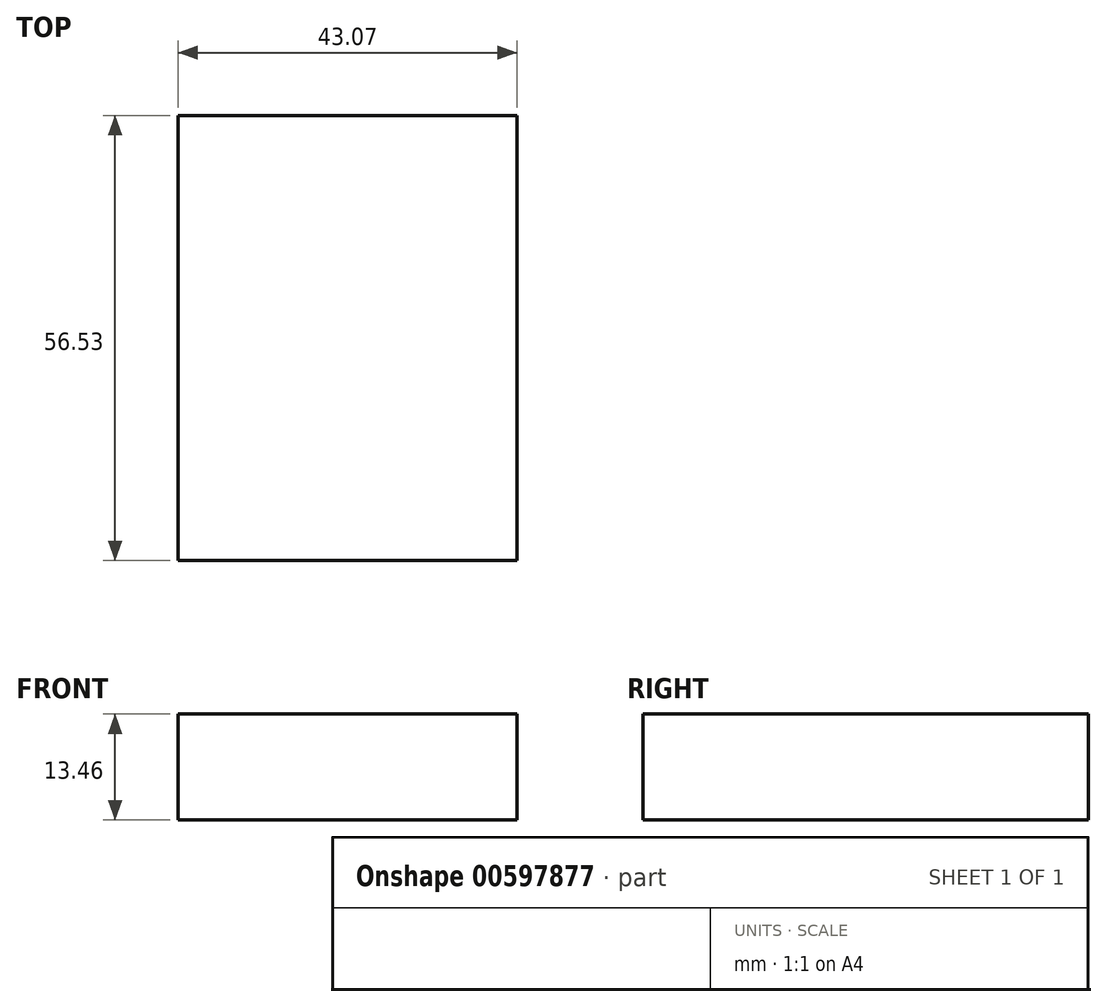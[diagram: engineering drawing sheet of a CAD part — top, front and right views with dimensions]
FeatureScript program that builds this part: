
annotation { "Feature Type Name" : "Feature", "Feature Type Description" : "" }
export const myFeature = defineFeature(function(context is Context, id is Id, definition is map)
    precondition{}
    {
        {
            var Q0;
            Q0=qCreatedBy(makeId("Top.planeOp"),FACE);
            var sketch = newSketch(context, id + "F0", { "sketchPlane" : qUnion([Q0])});
            skLineSegment(sketch, "E0.bottom", {"start": v(-17, -33.34) * mm, "end": v(26.06, -33.34) * mm});
            skLineSegment(sketch, "E0.top", {"start": v(-17, 23.2) * mm, "end": v(26.06, 23.2) * mm});
            skLineSegment(sketch, "E0.left", {"start": v(-17, -33.34) * mm, "end": v(-17, 23.2) * mm});
            skLineSegment(sketch, "E0.right", {"start": v(26.06, -33.34) * mm, "end": v(26.06, 23.2) * mm});
            skSolve(sketch);
        }
        {
            var Q0;
            Q0=makeQuery(id+"F0.imprint","IMPRINT",FACE,{"disambiguationData":[TD([[makeQuery(id+"F0.imprint","IMPRINT",EDGE,{"derivedFrom":sQuery(id+"F0.wireOp",EDGE,"E0.bottom")}),1.0]])]});
            extrude(context, id + "F1", {"entities" : qUnion([Q0]), "depth" : 13.46 * mm, "offsetDistance" : 25.4 * mm});
        }
    });
